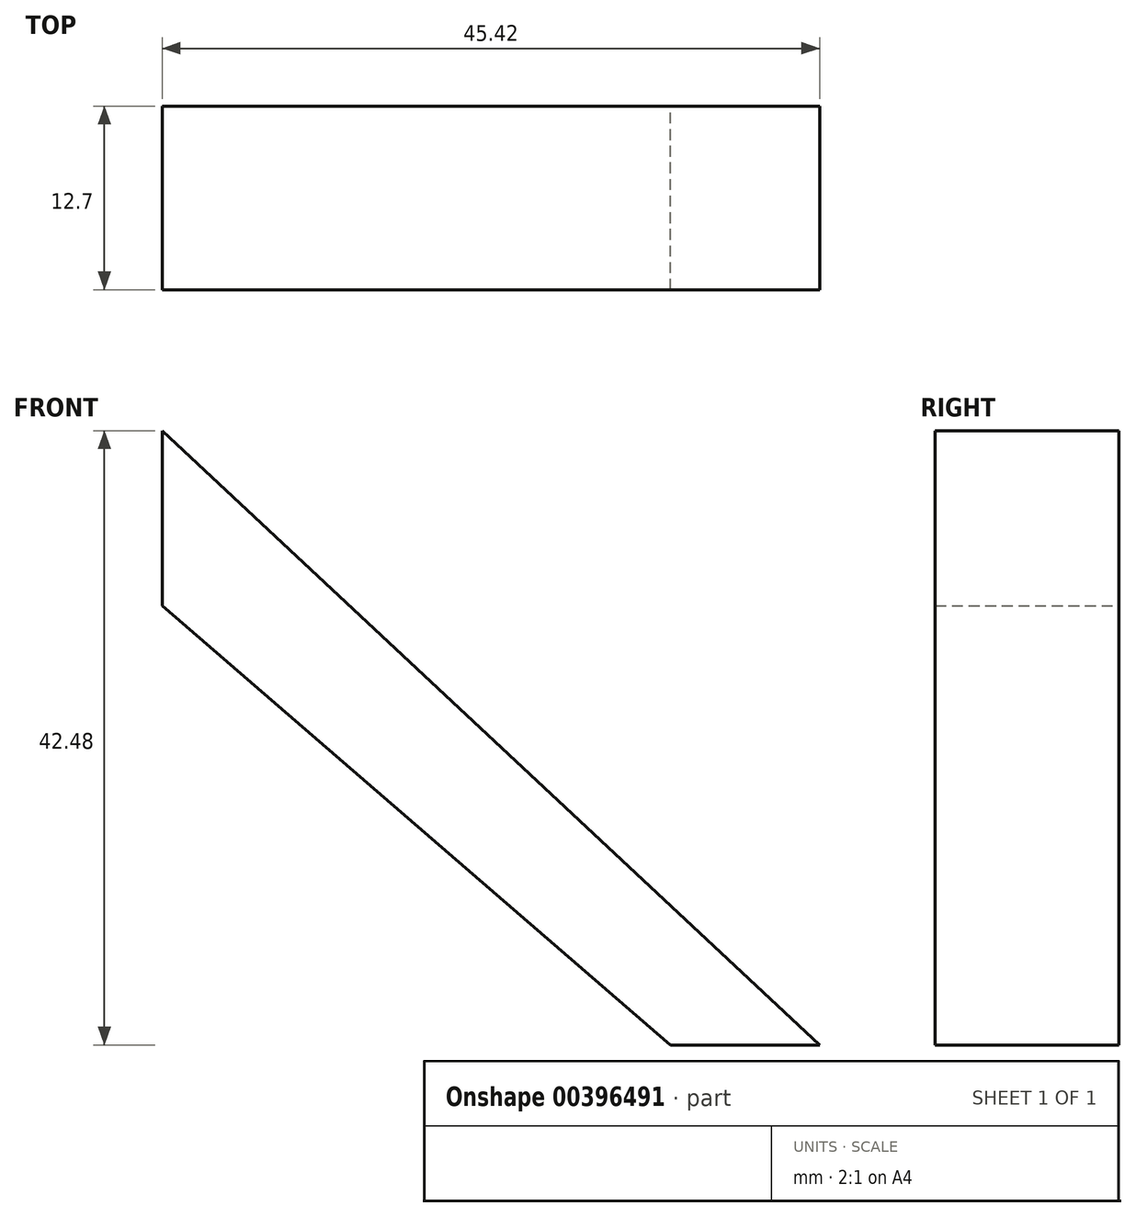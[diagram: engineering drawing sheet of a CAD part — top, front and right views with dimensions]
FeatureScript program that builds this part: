
annotation { "Feature Type Name" : "Feature", "Feature Type Description" : "" }
export const myFeature = defineFeature(function(context is Context, id is Id, definition is map)
    precondition{}
    {
        {
            var Q0;
            Q0=qCreatedBy(makeId("Front.planeOp"),FACE);
            var sketch = newSketch(context, id + "F0", { "sketchPlane" : qUnion([Q0])});
            skLineSegment(sketch, "E0", {"start": v(25.28, -18.21) * mm, "end": v(-20.14, 24.27) * mm});
            skLineSegment(sketch, "E1", {"start": v(-20.14, 24.27) * mm, "end": v(-20.14, 12.16) * mm});
            skLineSegment(sketch, "E2", {"start": v(-20.14, 12.16) * mm, "end": v(14.99, -18.21) * mm});
            skLineSegment(sketch, "E3", {"start": v(14.99, -18.21) * mm, "end": v(25.28, -18.21) * mm});
            skSolve(sketch);
        }
        {
            var Q0;
            Q0=makeQuery(id+"F0.imprint","IMPRINT",FACE,{"disambiguationData":[TD([[makeQuery(id+"F0.imprint","IMPRINT",EDGE,{"derivedFrom":sQuery(id+"F0.wireOp",EDGE,"E0")}),1.0]])]});
            extrude(context, id + "F1", {"entities" : qUnion([Q0]), "depth" : 12.7 * mm});
        }
    });
